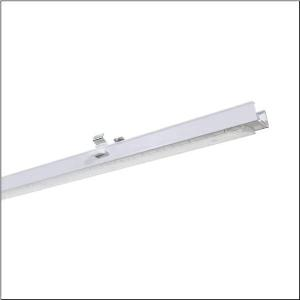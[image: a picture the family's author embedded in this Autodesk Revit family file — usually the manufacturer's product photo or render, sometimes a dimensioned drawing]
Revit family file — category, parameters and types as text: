
# Revit family: trunking_flex_31_51re11ma46b
name_source: partatom
category: Lighting Fixtures
units: mm (PartAtom-declared; Revit-internal decimal feet)

## family parameters
Cut with Voids When Loaded = No
Host = Face
Light Source = No
Part Type = Normal
Room Calculation Point = No
Round Connector Dimension = Use Diameter
Shared = No

## types (1)
- --- (1 x LED, 6400 lm, 40 W, 4000K)
    Apparent Load = 40 VA
    CIE Flux Codes = 83 93 98 100 100
    Color Rendering = 80
    Color Temperature = 4000K
    Default Elevation = 1800 mm
    Description = Trunking Flex 31, luminaire insert, of extruded aluminium section, coated, traffic white (RAL 9016), length: 1.172mm, width: 91mm, height: 53mm, LED rated luminous flux: 6.400lm, light colour: 840, SDCM (Standard Deviation of Colour Matching)MacAdam ≤ 3 SDCM (initial), control gear: ON/OFF Multilumen, with system connector: socket, mains connection: 220..240V, AC, 50/60Hz, rated input power: 40W, luminous flux adjustable on luminaire in four steps (3420/4540/5580/6630lm), connected load according to luminous flux setting (20/26/33/40W), primary light control with lens, of plastic, primary optical cover: cover, of PMMA, light emission: direct distribution, protection rating (complete): IP20, insulation class (complete): insulation class I (protective earthing), certification: CE, UKCA, impact resistance: IK02, permissible ambient temperature for indoor applications: -20..+40°C, packaging unit: 1 piece
    Height = 58 mm
    Lamp = 1 x LED
    Lamp Light Flux = 6400 lm
    Lamp Power = 40 W
    Lamp count = 1
    Length = 1172 mm
    Luminous efficacy = 160 lm/W
    Manufacturer = Siteco
    ModVariant = No
    Model = 51RE11MA46B
    Mounting Place = Ceiling
    Mounting Type = Pendant
    Number of Poles = 1
    OnlyDefault = Yes
    Power Factor = 1
    Product Name = Trunking Flex 31
    Product group = luminaire insert | ceiling pendant
    ProductGroupID = 901
    Protection Class = Protection class I
    Protection Degree = IP 20
    RLX_Detail_Level = 1
    RLX_Emergency_Light_Flux = 0 lm
    RLX_Emergency_Type = 0
    RLX_Emergency_Type_DB = No
    RlxData = <blob elided: 19945 chars, md5=d6879965>
    Socket = socket
    Standby Power = 0 W
    System Light Flux = 6400 lm
    System Power = 40 W
    Type Comments = factory setting: luminous flux: 100 % | (ON | ON) | 300 mA
    Type Image = l_1266702.jpg
    URL = http://relux.com
    VarID = @adj_067223
    Voltage = 0 V
    Weight = 0.00 kg
    Width = 65 mm

## geometry (parser evidence)
native form markers: Blend x4, Sweep x10
no freeform markers — native parametric forms only
